# Revit family: MINI_GAMMA-IP30-syst-UK-en
name_source: partatom
category: Electrical Equipment
units: mm (PartAtom-declared; Revit-internal decimal feet)

## family parameters
Cut with Voids When Loaded = No
Host = Face
Panel Configuration = Two Columns, Circuits Across
Part Type = Panelboard
Room Calculation Point = No
Round Connector Dimension = Use Diameter
Shared = No

## types (5) — shared parameters
EF000003 - Mounting method = EV000384 - Surface mounted (plaster)
EF000007 - Colour = EV000202 - White
EF000049 - Depth = 82 mm  [stored 0.269029 ft]
EF000116 - RAL-number = 9010
EF000118 - With mounting plate = No
EF000266 - Number of rows = 1
EF000339 - Type of cover = EV005746 - Optional
EF001062 - EMC-version = No
EF001088 - Extension possible = No
EF001131 - Internal depth = 82 mm  [stored 0.269029 ft]
EF001134 - DIN-rail = No
EF001596 - Material housing = EV000139 - Plastic
EF004462 - Type of closure = EV000154 - Other
EF005474 - Degree of protection (IP) = EV006410 - IP30
EF006244 - Transparent cover/door = No
EF006306 - With lock = No
EF009212 - Cover model = EV009916 - With notch
EF015776 - Earthing terminal block = No
EF015777 - Neutral terminal block = No
EF015941 - Signal passing door = No
HG000001 - Number of columns = 1
HG000002 - With door or cover = No
HG000003 - Range = mini gamma
HG000005 - Thickness = 3 mm  [stored 0.00984252 ft]
HG000006 - Flush mounted = No
HG000009 - Double swing door = No
HG000010 - Asymmetric doors = No
HG000011 - Empty rows from bottom = No
Manufacturer = Hager
Type Comments = mini gamma
zero-valued in all types: Default Elevation, EF000218 - Built-in depth, EF000332 - Built-in height, EF000846 - Built-in width, HG000007 - Number of empty columns, HG000008 - Number of empty rows

## per-type parameters (varying)
| type | EF000008 - Width | EF000040 - Height | EF002950 - Width in number of modular spacings | HG000004 - Manufacturer reference | Model |
| Surface mounted IP30 W110 H180 D82 4 Modular spacings - GD104E | 110 mm | 180 mm | 4 | GD104E | GD104E |
| Surface mounted IP30 W146 H180 D82 6 Modular spacings - GD106E | 146 mm | 180 mm | 6 | GD106E | GD106E |
| Surface mounted IP30 W182 H180 D82 8 Modular spacings - GD108E | 182 mm | 180 mm | 8 | GD108E | GD108E |
| Surface mounted IP30 W218 H180 D82 10 Modular spacings - GD110E | 218 mm | 180 mm | 10 | GD110E | GD110E |
| Surface mounted IP30 W55 H160 D82 2 Modular spacings - GD102E | 55 mm  [stored 0.180446 ft] | 160 mm  [stored 0.524934 ft] | 2 | GD102E | GD102E |

note: [stored X ft] marks values corroborated as IEEE doubles in the binary element streams (Revit-internal decimal feet)

## geometry (parser evidence)
native form markers: Sweep x12
no freeform markers — native parametric forms only
